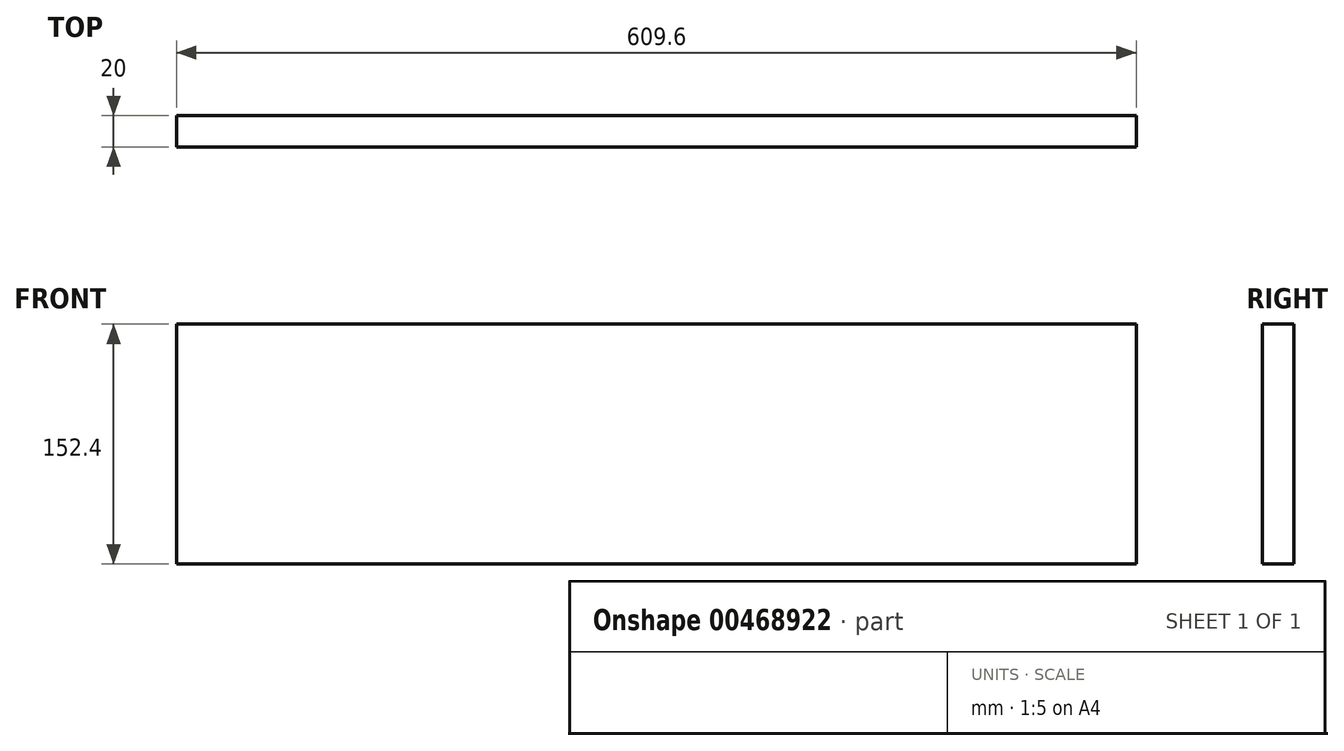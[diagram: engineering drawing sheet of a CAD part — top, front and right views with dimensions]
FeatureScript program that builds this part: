
annotation { "Feature Type Name" : "Feature", "Feature Type Description" : "" }
export const myFeature = defineFeature(function(context is Context, id is Id, definition is map)
    precondition{}
    {
        {
            var Q0;
            Q0=qCreatedBy(makeId("Front.planeOp"),FACE);
            var sketch = newSketch(context, id + "F0", { "sketchPlane" : qUnion([Q0])});
            skLineSegment(sketch, "E0.bottom", {"start": v(304.8, -76.2) * mm, "end": v(-304.8, -76.2) * mm});
            skLineSegment(sketch, "E0.top", {"start": v(304.8, 76.2) * mm, "end": v(-304.8, 76.2) * mm});
            skLineSegment(sketch, "E0.left", {"start": v(304.8, -76.2) * mm, "end": v(304.8, 76.2) * mm});
            skLineSegment(sketch, "E0.right", {"start": v(-304.8, -76.2) * mm, "end": v(-304.8, 76.2) * mm});
            skPoint(sketch, "E0.middle", {"position": v(0, 0) * mm});
            skSolve(sketch);
        }
        {
            var Q0;
            Q0=makeQuery(id+"F0.imprint","IMPRINT",FACE,{"disambiguationData":[TD([[makeQuery(id+"F0.imprint","IMPRINT",EDGE,{"derivedFrom":sQuery(id+"F0.wireOp",EDGE,"E0.bottom")}),-1.0]])]});
            extrude(context, id + "F1", {"entities" : qUnion([Q0]), "depth" : 20 * mm});
        }
    });
